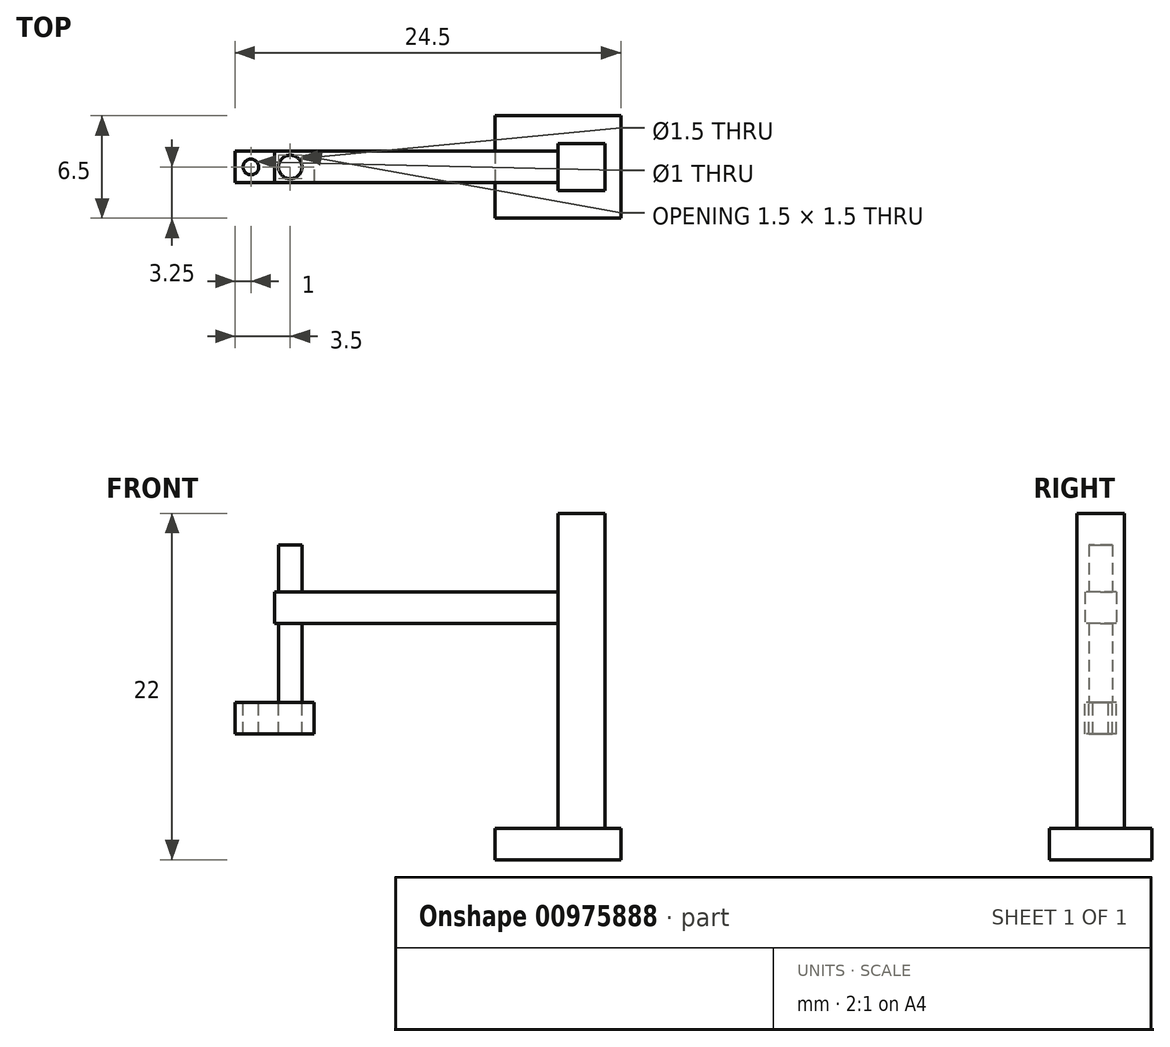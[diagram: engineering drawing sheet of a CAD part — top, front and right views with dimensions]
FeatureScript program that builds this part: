
annotation { "Feature Type Name" : "Feature", "Feature Type Description" : "" }
export const myFeature = defineFeature(function(context is Context, id is Id, definition is map)
    precondition{}
    {
        {
            var Q0;
            Q0=qCreatedBy(makeId("Top.planeOp"),FACE);
            var sketch = newSketch(context, id + "F0", { "sketchPlane" : qUnion([Q0])});
            skLineSegment(sketch, "E0.bottom", {"start": v(-4, 3.25) * mm, "end": v(4, 3.25) * mm});
            skLineSegment(sketch, "E0.top", {"start": v(-4, -3.25) * mm, "end": v(4, -3.25) * mm});
            skLineSegment(sketch, "E0.left", {"start": v(-4, 3.25) * mm, "end": v(-4, -3.25) * mm});
            skLineSegment(sketch, "E0.right", {"start": v(4, 3.25) * mm, "end": v(4, -3.25) * mm});
            skSolve(sketch);
        }
        {
            var Q0;
            Q0=makeQuery(id+"F0.imprint","IMPRINT",FACE,{"disambiguationData":[TD([[makeQuery(id+"F0.imprint","IMPRINT",EDGE,{"derivedFrom":sQuery(id+"F0.wireOp",EDGE,"E0.bottom")}),-1.0]])]});
            extrude(context, id + "F1", {"entities" : qUnion([Q0]), "depth" : 2 * mm, "offsetDistance" : 25 * mm});
        }
        {
            var Q0;
            Q0=makeQuery(id+"F1.opExtrude","CAP_FACE",FACE,{"disambiguationData":[OSD([sQuery(id+"F0.wireOp",EDGE,"E0.bottom"),sQuery(id+"F0.wireOp",EDGE,"E0.top"),sQuery(id+"F0.wireOp",EDGE,"E0.left"),sQuery(id+"F0.wireOp",EDGE,"E0.right")])],"isStart":false});
            var sketch = newSketch(context, id + "F2", { "sketchPlane" : qUnion([Q0])});
            skLineSegment(sketch, "E1", {"start": v(0, 0) * mm, "end": v(0, 1.5) * mm});
            skLineSegment(sketch, "E2.bottom", {"start": v(0, 1.5) * mm, "end": v(3, 1.5) * mm});
            skLineSegment(sketch, "E2.top", {"start": v(0, -1.5) * mm, "end": v(3, -1.5) * mm});
            skLineSegment(sketch, "E2.left", {"start": v(0, 1.5) * mm, "end": v(0, -1.5) * mm});
            skLineSegment(sketch, "E2.right", {"start": v(3, 1.5) * mm, "end": v(3, -1.5) * mm});
            skSolve(sketch);
        }
        {
            var Q0;
            {var subQ3=sQuery(id+"F2.wireOp",EDGE,"E2.bottom");Q0=makeQuery(id+"F2.imprint","IMPRINT",FACE,{"disambiguationData":[TD([[makeQuery(id+"F2.imprint","IMPRINT",EDGE,{"derivedFrom":subQ3}),-1.0]])]});}
            extrude(context, id + "F3", {"entities" : qUnion([Q0]), "operationType" : NewBodyOperationType.ADD, "depth" : 20 * mm, "offsetDistance" : 25 * mm});
        }
        {
            var Q0;
            Q0=qCreatedBy(makeId("Right.planeOp"),FACE);
            var sketch = newSketch(context, id + "F4", { "sketchPlane" : qUnion([Q0])});
            skLineSegment(sketch, "E3.bottom", {"start": v(1, 17) * mm, "end": v(-1, 17) * mm});
            skLineSegment(sketch, "E3.top", {"start": v(1, 15) * mm, "end": v(-1, 15) * mm});
            skLineSegment(sketch, "E3.left", {"start": v(1, 17) * mm, "end": v(1, 15) * mm});
            skLineSegment(sketch, "E3.right", {"start": v(-1, 17) * mm, "end": v(-1, 15) * mm});
            skSolve(sketch);
        }
        {
            var Q0;
            Q0=makeQuery(id+"F4.imprint","IMPRINT",FACE,{"disambiguationData":[TD([[makeQuery(id+"F4.imprint","IMPRINT",EDGE,{"derivedFrom":sQuery(id+"F4.wireOp",EDGE,"E3.bottom")}),1.0]])]});
            extrude(context, id + "F5", {"entities" : qUnion([Q0]), "operationType" : NewBodyOperationType.ADD, "oppositeDirection" : true, "depth" : 18 * mm, "offsetDistance" : 25 * mm});
        }
        {
            var Q0;
            Q0=makeQuery(id+"F5.opExtrude","SWEPT_FACE",FACE,{"disambiguationData":[OSD([sQuery(id+"F4.wireOp",EDGE,"E3.top")])]});
            var sketch = newSketch(context, id + "F6", { "sketchPlane" : qUnion([Q0])});
            skCircle(sketch, "E4", {"center": v(-17, 0) * mm, "radius": 0.75 * mm});
            skSolve(sketch);
        }
        {
            var Q0;
            Q0=makeQuery(id+"F6.imprint","IMPRINT",FACE,{"disambiguationData":[TD([[makeQuery(id+"F6.imprint","IMPRINT",EDGE,{"derivedFrom":sQuery(id+"F6.wireOp",EDGE,"E4")}),1.0]])]});
            extrude(context, id + "F7", {"entities" : qUnion([Q0]), "operationType" : NewBodyOperationType.ADD, "endBound" : BoundingType.SYMMETRIC, "oppositeDirection" : true, "depth" : 10 * mm, "offsetDistance" : 25 * mm});
        }
        {
            var Q0;
            Q0=makeQuery(id+"F7.opExtrude","CAP_FACE",FACE,{"disambiguationData":[OSD([sQuery(id+"F6.wireOp",EDGE,"E4")])],"isStart":true});
            var sketch = newSketch(context, id + "F8", { "sketchPlane" : qUnion([Q0])});
            skLineSegment(sketch, "E5.bottom", {"start": v(-15.5, -1) * mm, "end": v(-20.5, -1) * mm});
            skLineSegment(sketch, "E5.top", {"start": v(-15.5, 1) * mm, "end": v(-20.5, 1) * mm});
            skLineSegment(sketch, "E5.left", {"start": v(-15.5, -1) * mm, "end": v(-15.5, 1) * mm});
            skLineSegment(sketch, "E5.right", {"start": v(-20.5, -1) * mm, "end": v(-20.5, 1) * mm});
            skSolve(sketch);
        }
        {
            var Q0;
            Q0=makeQuery(id+"F8.imprint","IMPRINT",FACE,{"disambiguationData":[TD([[makeQuery(id+"F8.imprint","IMPRINT",EDGE,{"derivedFrom":sQuery(id+"F8.wireOp",EDGE,"E5.bottom")}),-1.0]])]});
            extrude(context, id + "F9", {"entities" : qUnion([Q0]), "depth" : 2 * mm, "offsetDistance" : 25 * mm});
        }
        {
            var Q0;
            Q0=makeQuery(id+"F9.opExtrude","CAP_FACE",FACE,{"disambiguationData":[OSD([sQuery(id+"F6.wireOp",EDGE,"E4"),sQuery(id+"F8.wireOp",EDGE,"E5.bottom"),sQuery(id+"F8.wireOp",EDGE,"E5.top"),sQuery(id+"F8.wireOp",EDGE,"E5.left"),sQuery(id+"F8.wireOp",EDGE,"E5.right")])],"isStart":true});
            var sketch = newSketch(context, id + "F10", { "sketchPlane" : qUnion([Q0])});
            skCircle(sketch, "E6", {"center": v(-19.5, 0) * mm, "radius": 0.5 * mm});
            skSolve(sketch);
        }
        {
            var Q0;
            Q0=makeQuery(id+"F10.imprint","IMPRINT",FACE,{"disambiguationData":[TD([[makeQuery(id+"F10.imprint","IMPRINT",EDGE,{"derivedFrom":sQuery(id+"F10.wireOp",EDGE,"E6")}),1.0]])]});
            extrude(context, id + "F11", {"entities" : qUnion([Q0]), "operationType" : NewBodyOperationType.REMOVE, "oppositeDirection" : true, "depth" : 25 * mm, "offsetDistance" : 25 * mm});
        }
    });
